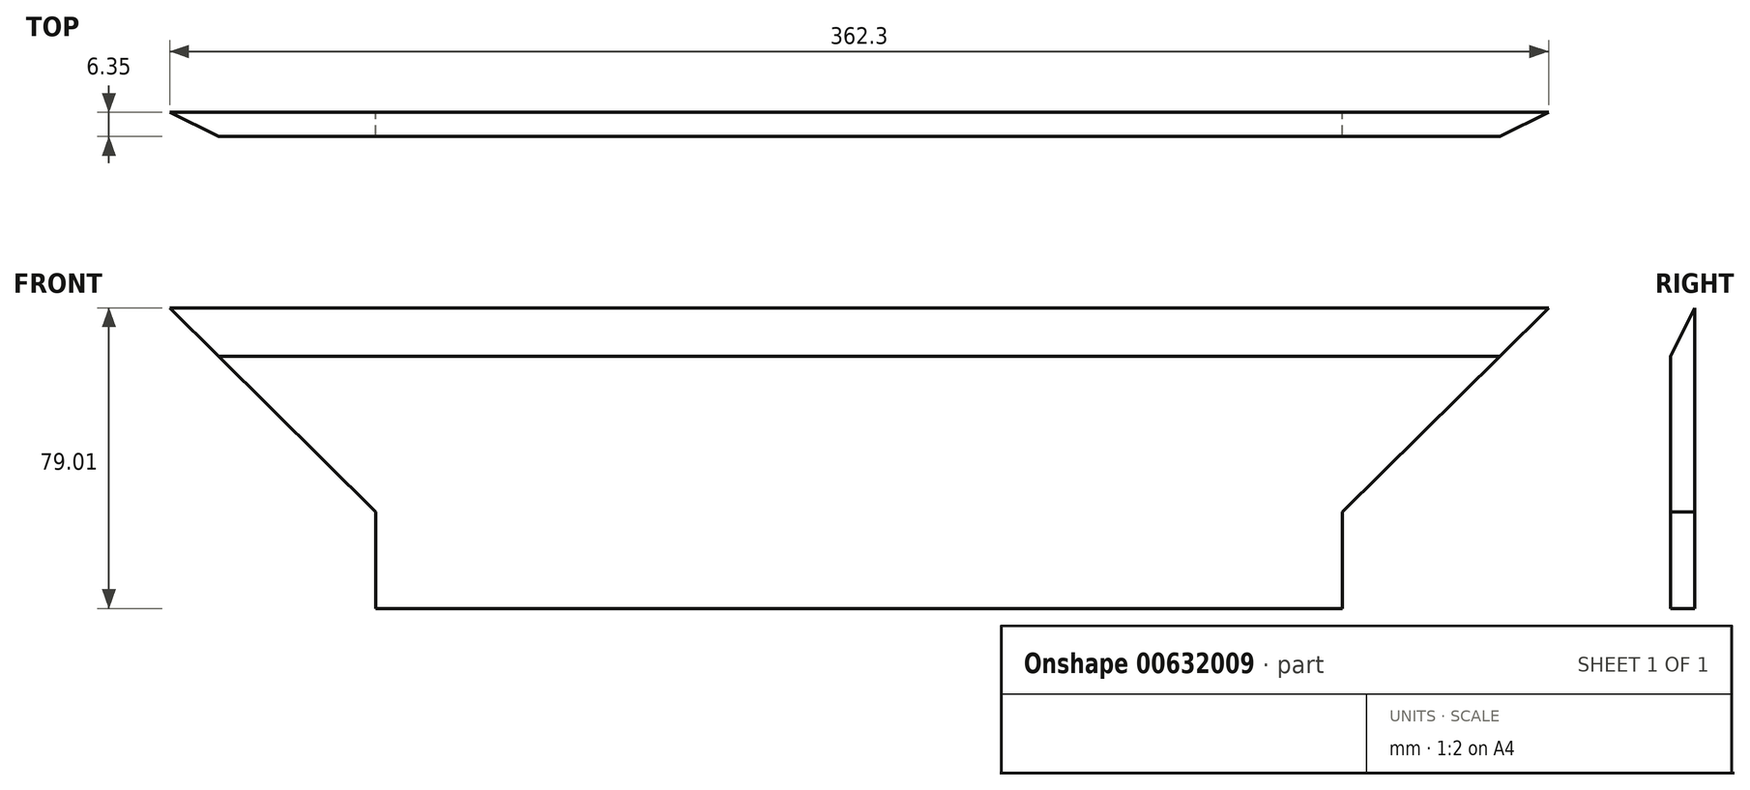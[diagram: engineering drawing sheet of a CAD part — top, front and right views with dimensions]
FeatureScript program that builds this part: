
annotation { "Feature Type Name" : "Feature", "Feature Type Description" : "" }
export const myFeature = defineFeature(function(context is Context, id is Id, definition is map)
    precondition{}
    {
        {
            var Q0;
            Q0=qCreatedBy(makeId("Front.planeOp"),FACE);
            var sketch = newSketch(context, id + "F0", { "sketchPlane" : qUnion([Q0])});
            skLineSegment(sketch, "E0.bottom", {"start": v(0, 0) * mm, "end": v(254, 0) * mm});
            skLineSegment(sketch, "E0.top", {"start": v(0, 25.4) * mm, "end": v(254, 25.4) * mm});
            skLineSegment(sketch, "E0.left", {"start": v(0, 0) * mm, "end": v(0, 25.4) * mm});
            skLineSegment(sketch, "E0.right", {"start": v(254, 0) * mm, "end": v(254, 25.4) * mm});
            skLineSegment(sketch, "E1", {"start": v(0, 25.4) * mm, "end": v(-54.15, 79.01) * mm});
            skLineSegment(sketch, "E2", {"start": v(-54.15, 79.01) * mm, "end": v(308.15, 79.01) * mm});
            skLineSegment(sketch, "E3", {"start": v(308.15, 79.01) * mm, "end": v(254, 25.4) * mm});
            skSolve(sketch);
        }
        {
            var Q0;
            Q0=makeQuery(id+"F0.imprint","IMPRINT",FACE,{"disambiguationData":[TD([[makeQuery(id+"F0.imprint","IMPRINT",EDGE,{"derivedFrom":sQuery(id+"F0.wireOp",EDGE,"E0.bottom")}),1.0]])]});
            var Q1;
            Q1=makeQuery(id+"F0.imprint","IMPRINT",FACE,{"disambiguationData":[TD([[makeQuery(id+"F0.imprint","IMPRINT",EDGE,{"derivedFrom":sQuery(id+"F0.wireOp",EDGE,"E0.top")}),1.0]])]});
            extrude(context, id + "F1", {"entities" : qUnion([Q0, Q1]), "depth" : 6.35 * mm, "offsetDistance" : 25.4 * mm});
        }
        {
            var Q0;
            Q0=makeQuery(id+"F1.opExtrude","CAP_EDGE",EDGE,{"disambiguationData":[OSD([sQuery(id+"F0.wireOp",EDGE,"E2")])],"isStart":false});
            chamfer(context, id + "F2", {"entities" : qUnion([Q0]), "chamferType" : ChamferType.TWO_OFFSETS, "width1" : 6.35 * mm, "oppositeDirection" : false, "width2" : 12.7 * mm, "tangentPropagation" : true});
        }
    });
